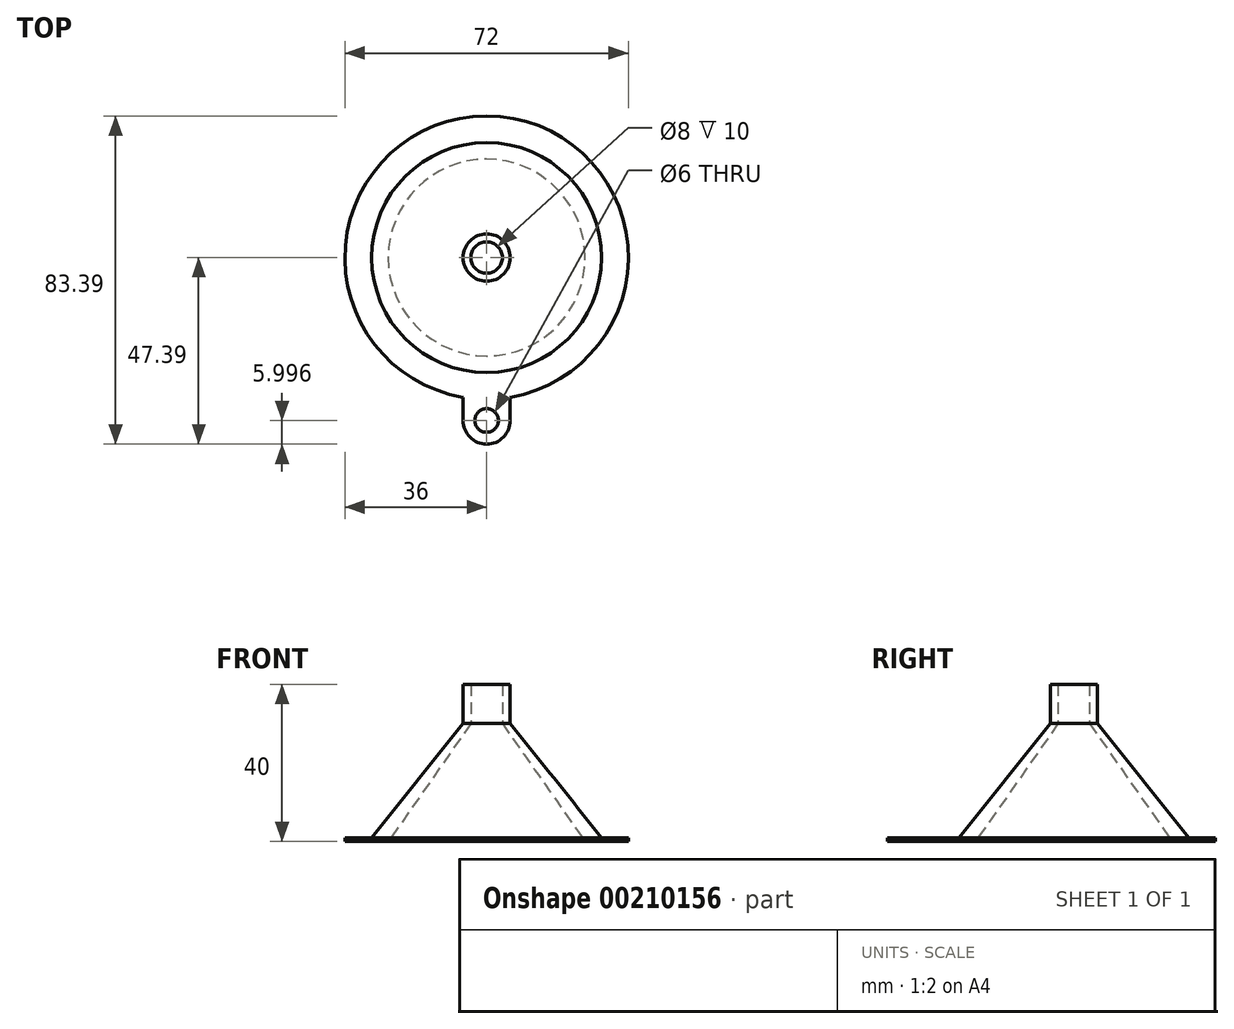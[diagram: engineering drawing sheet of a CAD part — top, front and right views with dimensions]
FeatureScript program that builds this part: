
annotation { "Feature Type Name" : "Feature", "Feature Type Description" : "" }
export const myFeature = defineFeature(function(context is Context, id is Id, definition is map)
    precondition{}
    {
        {
            var Q0;
            Q0=qCreatedBy(makeId("Top.planeOp"),FACE);
            var sketch = newSketch(context, id + "F0", { "sketchPlane" : qUnion([Q0])});
            skCircle(sketch, "E0", {"center": v(0, 0) * mm, "radius": 30 * mm});
            skSolve(sketch);
        }
        {
            var Q0;
            Q0=qCreatedBy(makeId("Top.planeOp"),FACE);
            cPlane(context, id + "F1", {"entities" : qUnion([Q0]), "cplaneType" : CPlaneType.OFFSET, "offset" : 30 * mm, "width" : 150 * mm, "height" : 150 * mm});
        }
        {
            var Q0;
            Q0=qCreatedBy(id+"F1.planeOp",FACE);
            var sketch = newSketch(context, id + "F2", { "sketchPlane" : qUnion([Q0])});
            skCircle(sketch, "E1", {"center": v(0, 0) * mm, "radius": 6 * mm});
            skSolve(sketch);
        }
        {
            var Q0;
            Q0=makeQuery(id+"F0.imprint","IMPRINT",FACE,{"disambiguationData":[TD([[makeQuery(id+"F0.imprint","IMPRINT",EDGE,{"derivedFrom":sQuery(id+"F0.wireOp",EDGE,"E0")}),1.0]])]});
            var Q1;
            Q1=makeQuery(id+"F2.imprint","IMPRINT",FACE,{"disambiguationData":[TD([[makeQuery(id+"F2.imprint","IMPRINT",EDGE,{"derivedFrom":sQuery(id+"F2.wireOp",EDGE,"E1")}),1.0]])]});
            loft(context, id + "F3", {"sheetProfilesArray" : [{ "sheetProfileEntities" : qUnion([Q0]) }, { "sheetProfileEntities" : qUnion([Q1]) }]});
        }
        {
            var Q0;
            Q0=qCreatedBy(makeId("Top.planeOp"),FACE);
            var sketch = newSketch(context, id + "F4", { "sketchPlane" : qUnion([Q0])});
            skCircle(sketch, "E2", {"center": v(0, 0) * mm, "radius": 25 * mm});
            skSolve(sketch);
        }
        {
            var Q0;
            Q0=qCreatedBy(id+"F1.planeOp",FACE);
            var sketch = newSketch(context, id + "F5", { "sketchPlane" : qUnion([Q0])});
            skCircle(sketch, "E3", {"center": v(0, 0) * mm, "radius": 4 * mm});
            skSolve(sketch);
        }
        {
            var Q1;
            Q1 = qSketchRegion(id + "F4", true);
            var Q2;
            Q2 = qSketchRegion(id + "F5", true);
            loft(context, id + "F6", {"operationType" : NewBodyOperationType.REMOVE, "sheetProfilesArray" : [{ "sheetProfileEntities" : qUnion([Q1]) }, { "sheetProfileEntities" : qUnion([Q2]) }]});
        }
        {
            var Q0;
            Q0=makeQuery(id+"F3.opLoft","CAP_FACE",FACE,{"disambiguationData":[OSD([makeQuery(id+"F2.imprint","IMPRINT",FACE,{"disambiguationData":[TD([[makeQuery(id+"F2.imprint","IMPRINT",EDGE,{"derivedFrom":sQuery(id+"F2.wireOp",EDGE,"E1")}),1.0]])]})])],"isStart":true});
            var sketch = newSketch(context, id + "F7", { "sketchPlane" : qUnion([Q0])});
            skCircle(sketch, "E4.0", {"center": v(0, 0) * mm, "radius": 6 * mm});
            skCircle(sketch, "E4.1", {"center": v(0, 0) * mm, "radius": 4 * mm});
            skSolve(sketch);
        }
        {
            var Q0;
            Q0=makeQuery(id+"F7.imprint","IMPRINT",FACE,{"disambiguationData":[TD([[makeQuery(id+"F7.imprint","IMPRINT",EDGE,{"derivedFrom":sQuery(id+"F7.wireOp",EDGE,"E4.0")}),1.0]])]});
            extrude(context, id + "F8", {"entities" : qUnion([Q0]), "operationType" : NewBodyOperationType.ADD, "depth" : 10 * mm});
        }
        {
            var Q0;
            Q0=qCreatedBy(makeId("Top.planeOp"),FACE);
            var sketch = newSketch(context, id + "F9", { "sketchPlane" : qUnion([Q0])});
            skCircle(sketch, "E5.0", {"center": v(0, 0) * mm, "radius": 27 * mm});
            skLineSegment(sketch, "E6.left", {"start": v(-6, -35.5) * mm, "end": v(-6, -41.4) * mm});
            skLineSegment(sketch, "E6.right", {"start": v(6, -35.5) * mm, "end": v(6, -41.4) * mm});
            skArc(sketch, "E7", {"start": v(-6, -41.4) * mm, "mid": v(0, -47.4) * mm, "end": v(6, -41.4) * mm});
            skCircle(sketch, "E8", {"center": v(0, -41.4) * mm, "radius": 3 * mm});
            skCircle(sketch, "E9.0", {"center": v(0, 0) * mm, "radius": 30 * mm, "construction": true});
            skArc(sketch, "E10.0", {"start": v(6, -35.5) * mm, "mid": v(0, 36) * mm, "end": v(-6, -35.5) * mm});
            skPoint(sketch, "E11.orphan", {"position": v(6, -29.4) * mm});
            skSolve(sketch);
        }
        {
            var Q0;
            Q0=makeQuery(id+"F9.imprint","IMPRINT",FACE,{"disambiguationData":[TD([[makeQuery(id+"F9.imprint","IMPRINT",EDGE,{"derivedFrom":sQuery(id+"F9.wireOp",EDGE,"E5.0")}),-1.0]])]});
            extrude(context, id + "F10", {"entities" : qUnion([Q0]), "operationType" : NewBodyOperationType.ADD, "depth" : 1 * mm});
        }
    });
